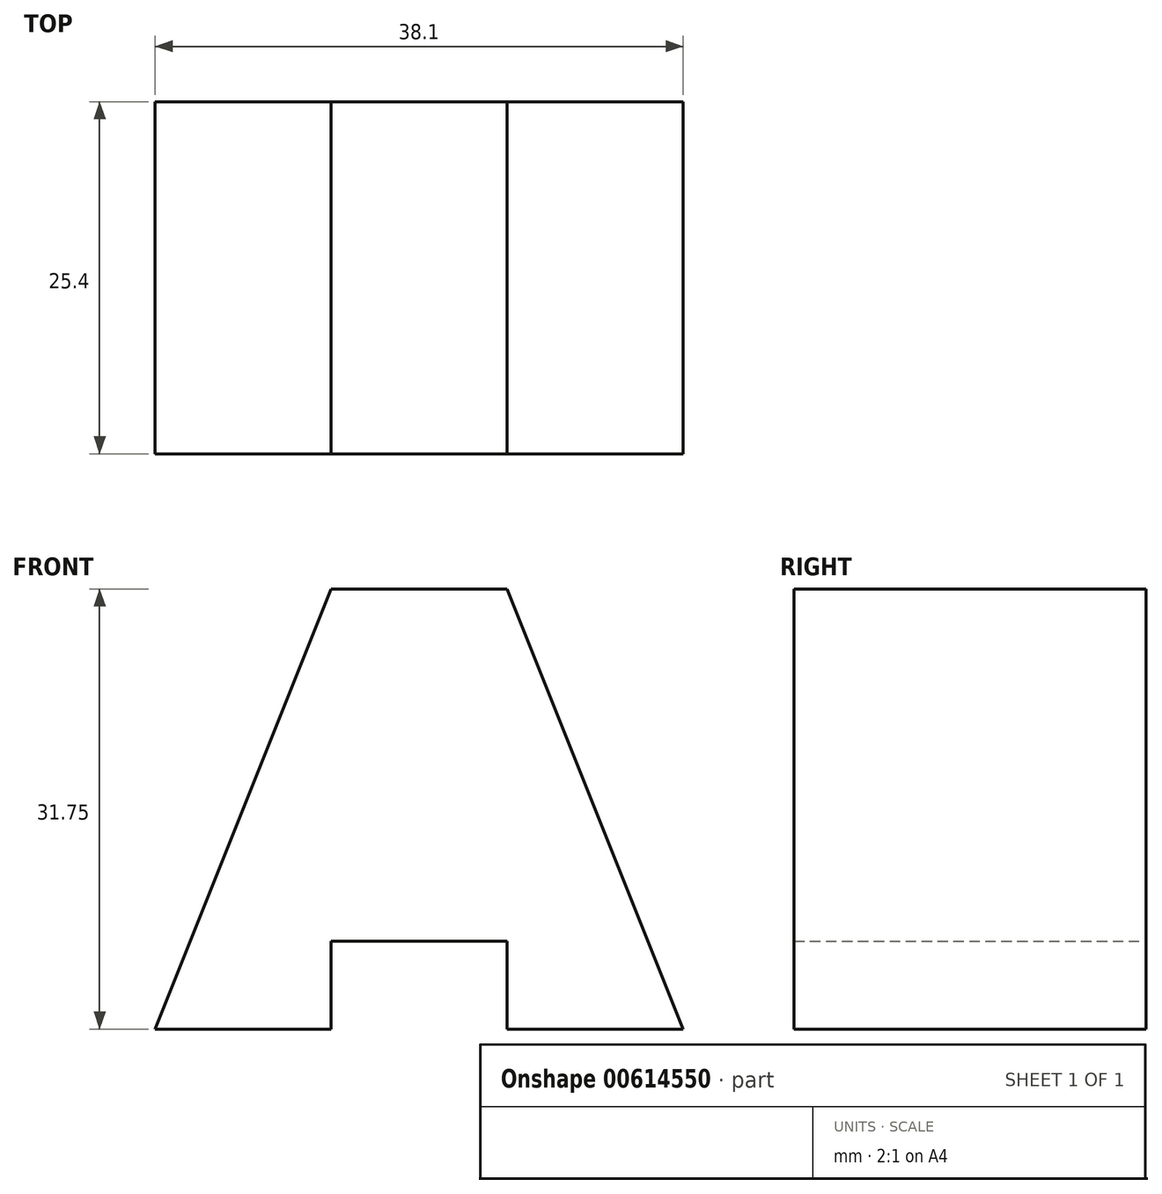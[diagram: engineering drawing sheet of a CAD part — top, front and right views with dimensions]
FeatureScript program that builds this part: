
annotation { "Feature Type Name" : "Feature", "Feature Type Description" : "" }
export const myFeature = defineFeature(function(context is Context, id is Id, definition is map)
    precondition{}
    {
        {
            var Q0;
            Q0=qCreatedBy(makeId("Front.planeOp"),FACE);
            var sketch = newSketch(context, id + "F0", { "sketchPlane" : qUnion([Q0])});
            skLineSegment(sketch, "E0", {"start": v(0, 0) * mm, "end": v(12.7, 0) * mm});
            skLineSegment(sketch, "E1", {"start": v(25.4, 0) * mm, "end": v(38.1, 0) * mm});
            skLineSegment(sketch, "E2", {"start": v(12.7, 0) * mm, "end": v(12.7, 6.35) * mm});
            skLineSegment(sketch, "E3", {"start": v(25.4, 0) * mm, "end": v(25.4, 6.35) * mm});
            skLineSegment(sketch, "E4", {"start": v(12.7, 6.35) * mm, "end": v(25.4, 6.35) * mm});
            skLineSegment(sketch, "E5", {"start": v(12.7, 31.75) * mm, "end": v(25.4, 31.75) * mm});
            skLineSegment(sketch, "E6", {"start": v(12.7, 31.75) * mm, "end": v(0, 0) * mm});
            skLineSegment(sketch, "E7", {"start": v(25.4, 31.75) * mm, "end": v(38.1, 0) * mm});
            skSolve(sketch);
        }
        {
            var Q0;
            Q0=makeQuery(id+"F0.imprint","IMPRINT",FACE,{"disambiguationData":[TD([[makeQuery(id+"F0.imprint","IMPRINT",EDGE,{"derivedFrom":sQuery(id+"F0.wireOp",EDGE,"E0")}),1.0]])]});
            extrude(context, id + "F1", {"entities" : qUnion([Q0]), "depth" : 25.4 * mm, "offsetDistance" : 25.4 * mm});
        }
    });
